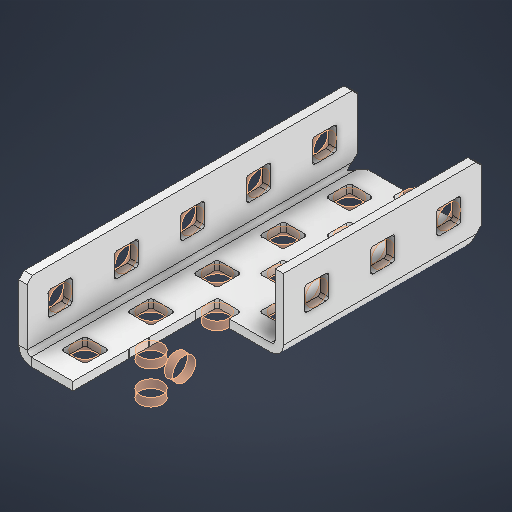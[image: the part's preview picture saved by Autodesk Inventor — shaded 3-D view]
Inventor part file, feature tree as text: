
AUTODESK INVENTOR PART (.ipt)
format: ipt  version: 2025.2 (Build 292293000, 293)  size: 710,144 bytes
history: native  units: in
note: dims shown in document units (in); Inventor stores cm internally (conversion verified against a paired STEP export)
features: other x32, extrude x24, sheet_metal_op x11, sketch x4, pattern_linear x2, mirror x1, chamfer x1
ambient origin geometry x8: Origin, YZ Plane, XZ Plane, XY Plane, X Axis, Y Axis, Z Axis, Center Point
bodies: Solid1 (feature_tree), Body (feature_tree)
feature tree (75):
  sheet_metal_op  "Flanges"
  other  "Flange Pattern Plane"
  other  "Flange Pattern Sketch"
  sheet_metal_op  "Flange Pattern"
  sheet_metal_op  "Body Pattern"
  pattern_linear  "Center Pattern"  Spacing1=0.0312in  [1 undecoded]
  other  "Arc Length"
  mirror  "Notch Mirror"
  pattern_linear  "Notch Pattern"  Spacing1=0.125in  [1 undecoded]
  chamfer  "End Chamfer"
  extrude  "Half Cut"  Depth=0.0625in
  extrude  "Extrusion2"  Depth=0.5in TaperAngle=90.0deg
  other  "Plate1"
  sketch  "Sketch2"  dims[d1=2.5in]
  other  "Plate2"
  sheet_metal_op  "Bend1"
  sheet_metal_op  "Corner1"
  sketch  "Sketch Rectangular Pattern1"  dims[d0=1.0in]
  other  "Srf1"
  other  "Srf2"
  other  "Srf91"
  sheet_metal_op  "Body Pattern Sketch"
  sketch  "Sketch Rectangular Pattern2"  dims[d2=0.0625in]
  other  "Srf92"
  other  "Srf786"
  other  "Srf823"
  other  "Srf824"
  other  "Srf825"
  other  "Srf826"
  other  "Srf827"
  other  "Srf828"
  other  "Srf829"
  other  "Srf856"
  other  "Srf857"
  other  "Srf858"
  other  "Srf859"
  other  "Srf860"
  other  "Srf861"
  other  "Srf862"
  other  "Srf889"
  other  "Srf890"
  other  "Srf891"
  other  "Srf892"
  other  "Srf922"
  other  "Srf959"
  sketch  "Sketch17"  dims[d3=0.0625in d4=0.0312in d5=0.125in d6=0.0625in d7=0.5in d8=90.0deg d9=0.0312in d10=0.25in d11=0.0625in d12=0.0625in d16=0.182in d17=0.02in d18=0.0625in d19=0.0in d20=0.25in d21=0.25in d38=1.9685in d40=0.5in d41=0.7874in d43=1.0in d46=0.172in d47=1.0in d48=0.0in d49=0.182in d50=0.02in d51=0.25in d52=0.25in d53=0.0625in d54=0.0in d55=0.172in d56=1.0in d57=0.0in d58=0.25in d60=1.9685in d62=0.5in d63=0.7874in d65=0.5in d85=0.1473in d86=0.1782in d88=0.04in d89=0.0625in d90=0.0in d91=0.04in d92=0.0491in d95=2.5in d96=0.04in d97=0.25in d98=45.0deg d99=0.25in d100=0.5in d101=0.0in d102=2.497in d106=0.182in d107=0.02in d108=0.5in d109=0.5in d110=0.0625in d111=0.0in d112=0.172in d113=0.5in d114=0.0in d117=0.5in d118=0.5in d119=0.5in d121=1.0in d122=0.59in d123=0.0in d124=0.5in d125=0.0344in]
  sheet_metal_op  "Flange Stamp"
  sheet_metal_op  "Flange Circle"
  sheet_metal_op  "Body Stamp"
  sheet_metal_op  "Body Circle"
  other  "Center Stamp"
  other  "Center Circle"
  sheet_metal_op  "Notch"
  extrude  "ExtrusionSrf2"  Depth=0.5in
  extrude  "ExtrusionSrf92"  Depth=0.0625in
  extrude  "ExtrusionSrf823"  Depth=0.0625in
  extrude  "ExtrusionSrf824"  Depth=0.5in
  extrude  "ExtrusionSrf825"  Depth=0.02in
  extrude  "ExtrusionSrf826"  Depth=0.0625in
  extrude  "ExtrusionSrf827"  TaperAngle=0.0deg  [1 undecoded]
  extrude  "ExtrusionSrf828"  Depth=0.5in
  extrude  "ExtrusionSrf829"  Depth=0.5in
  extrude  "ExtrusionSrf856"  Depth=0.5in
  extrude  "ExtrusionSrf857"  Depth=0.5in
  extrude  "ExtrusionSrf858"  Depth=1.0in TaperAngle=0.0deg
  extrude  "ExtrusionSrf859"  Depth=0.5in
  extrude  "ExtrusionSrf860"  Depth=0.02in
  extrude  "ExtrusionSrf861"  Depth=0.5in
  extrude  "ExtrusionSrf862"  Depth=0.5in
  extrude  "ExtrusionSrf889"  Depth=0.0625in
  extrude  "ExtrusionSrf890"  TaperAngle=0.0deg  [1 undecoded]
  extrude  "ExtrusionSrf891"  Depth=0.5in
  extrude  "ExtrusionSrf892"  Depth=1.0in TaperAngle=0.0deg
  extrude  "ExtrusionSrf922"  Depth=0.5in
  extrude  "ExtrusionSrf959"  Depth=0.5in
note: 4 required parameter values undecoded (feature->parameter linkage not recoverable at this tier; creation-order binding heuristic only, values carry confidence <= 0.55)
